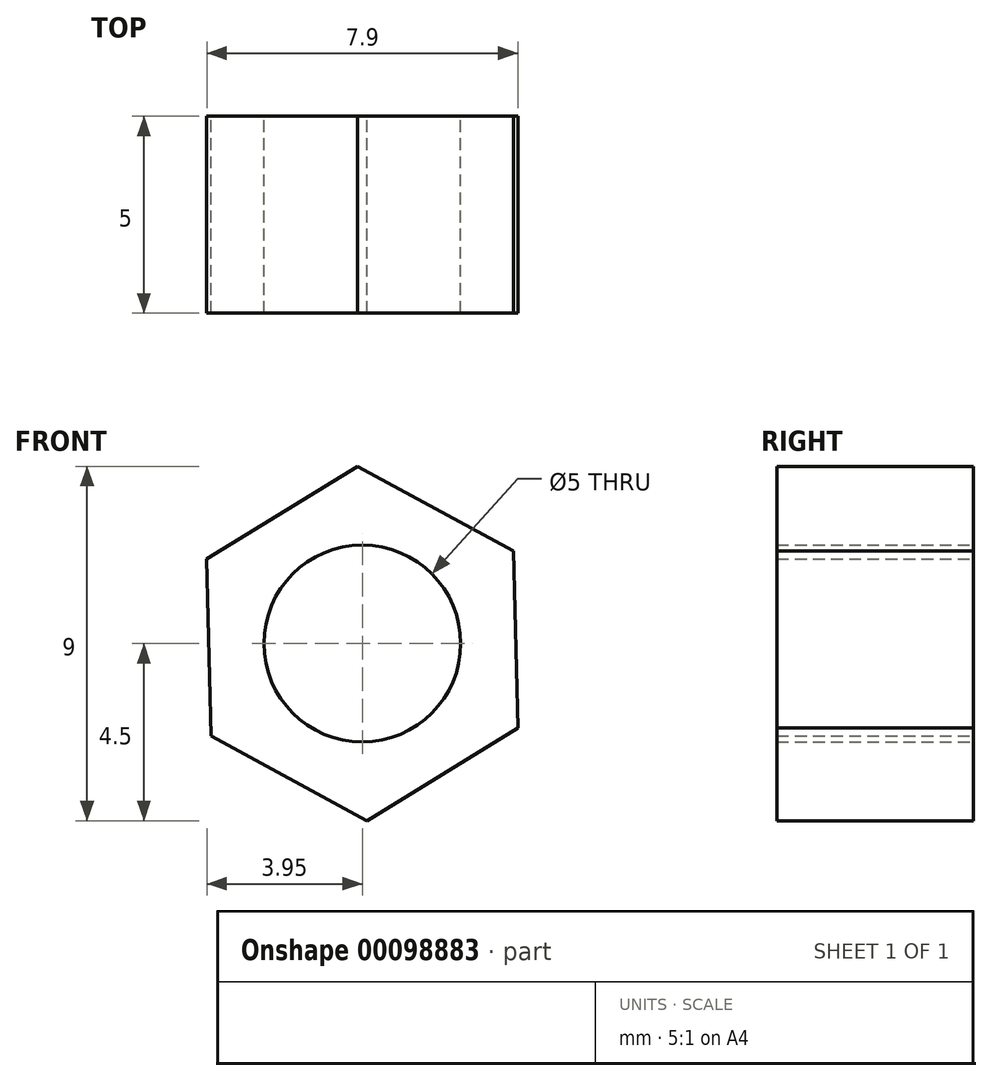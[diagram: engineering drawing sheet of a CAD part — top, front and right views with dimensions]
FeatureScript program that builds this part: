
annotation { "Feature Type Name" : "Feature", "Feature Type Description" : "" }
export const myFeature = defineFeature(function(context is Context, id is Id, definition is map)
    precondition{}
    {
        {
            var Q0;
            Q0=qCreatedBy(makeId("Front.planeOp"),FACE);
            var sketch = newSketch(context, id + "F0", { "sketchPlane" : qUnion([Q0])});
            skCircle(sketch, "E0", {"center": v(0, 0) * mm, "radius": 2.5 * mm});
            skCircle(sketch, "E1.cCircle", {"center": v(0, 0) * mm, "radius": 4.5 * mm, "construction": true});
            skLineSegment(sketch, "E1.0", {"start": v(3.84, 2.35) * mm, "end": v(3.95, -2.15) * mm});
            skLineSegment(sketch, "E1.1", {"start": v(3.95, -2.15) * mm, "end": v(0.12, -4.5) * mm});
            skLineSegment(sketch, "E1.2", {"start": v(0.12, -4.5) * mm, "end": v(-3.84, -2.35) * mm});
            skLineSegment(sketch, "E1.3", {"start": v(-3.84, -2.35) * mm, "end": v(-3.95, 2.15) * mm});
            skLineSegment(sketch, "E1.4", {"start": v(-3.95, 2.15) * mm, "end": v(-0.12, 4.5) * mm});
            skLineSegment(sketch, "E1.5", {"start": v(-0.12, 4.5) * mm, "end": v(3.84, 2.35) * mm});
            skSolve(sketch);
        }
        {
            var Q0;
            Q0=makeQuery(id+"F0.imprint","IMPRINT",FACE,{"disambiguationData":[TD([[makeQuery(id+"F0.imprint","IMPRINT",EDGE,{"derivedFrom":sQuery(id+"F0.wireOp",EDGE,"E0")}),-1.0]])]});
            extrude(context, id + "F1", {"entities" : qUnion([Q0]), "depth" : 5 * mm});
        }
    });
